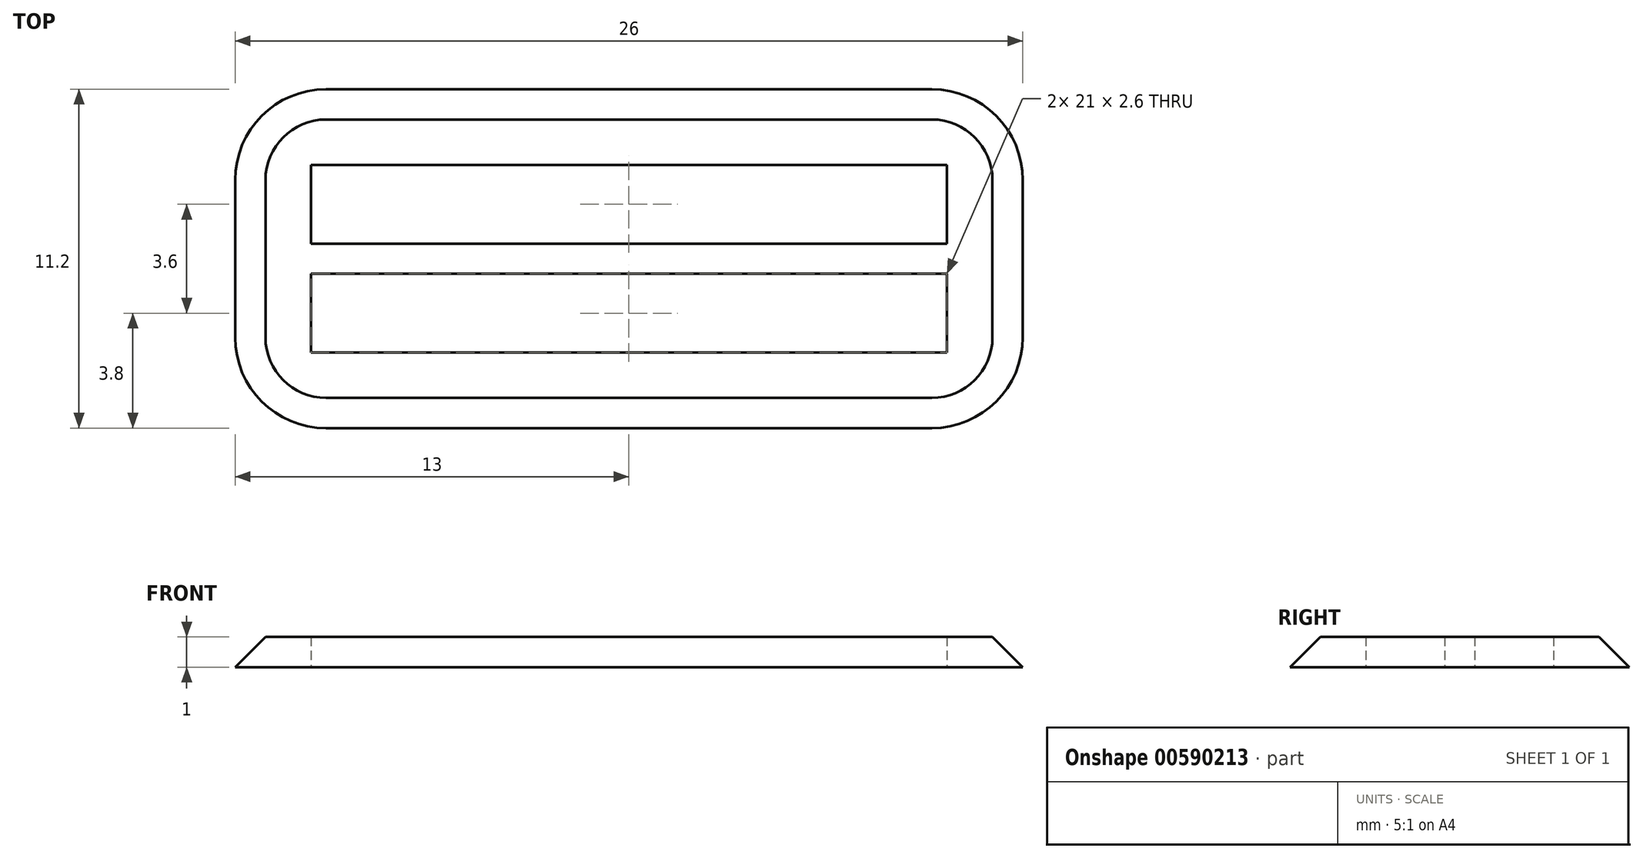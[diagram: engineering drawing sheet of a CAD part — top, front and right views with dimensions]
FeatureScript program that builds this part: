
annotation { "Feature Type Name" : "Feature", "Feature Type Description" : "" }
export const myFeature = defineFeature(function(context is Context, id is Id, definition is map)
    precondition{}
    {
        {
            var Q0;
            Q0=qCreatedBy(makeId("Top.planeOp"),FACE);
            var sketch = newSketch(context, id + "F0", { "sketchPlane" : qUnion([Q0])});
            skPoint(sketch, "E0.middle", {"position": v(0, 0) * mm});
            skLineSegment(sketch, "E1.bottom", {"start": v(-10.5, 3.1) * mm, "end": v(10.5, 3.1) * mm});
            skLineSegment(sketch, "E1.top", {"start": v(-10.5, 0.5) * mm, "end": v(10.5, 0.5) * mm});
            skLineSegment(sketch, "E1.left", {"start": v(-10.5, 3.1) * mm, "end": v(-10.5, 0.5) * mm});
            skLineSegment(sketch, "E1.right", {"start": v(10.5, 3.1) * mm, "end": v(10.5, 0.5) * mm});
            skPoint(sketch, "E1.middle", {"position": v(0, 1.8) * mm});
            skLineSegment(sketch, "E2.bottom", {"start": v(-10.5, -0.5) * mm, "end": v(10.5, -0.5) * mm});
            skLineSegment(sketch, "E2.top", {"start": v(-10.5, -3.1) * mm, "end": v(10.5, -3.1) * mm});
            skLineSegment(sketch, "E2.left", {"start": v(-10.5, -0.5) * mm, "end": v(-10.5, -3.1) * mm});
            skLineSegment(sketch, "E2.right", {"start": v(10.5, -0.5) * mm, "end": v(10.5, -3.1) * mm});
            skPoint(sketch, "E2.middle", {"position": v(0, -1.8) * mm});
            skLineSegment(sketch, "E3.bottom", {"start": v(-13, 5.6) * mm, "end": v(13, 5.6) * mm});
            skLineSegment(sketch, "E3.top", {"start": v(-13, -5.6) * mm, "end": v(13, -5.6) * mm});
            skLineSegment(sketch, "E3.left", {"start": v(-13, 5.6) * mm, "end": v(-13, -5.6) * mm});
            skLineSegment(sketch, "E3.right", {"start": v(13, 5.6) * mm, "end": v(13, -5.6) * mm});
            skSolve(sketch);
        }
        {
            var Q0;
            Q0=makeQuery(id+"F0.imprint","IMPRINT",FACE,{"disambiguationData":[TD([[makeQuery(id+"F0.imprint","IMPRINT",EDGE,{"derivedFrom":sQuery(id+"F0.wireOp",EDGE,"E1.bottom")}),1.0]])]});
            extrude(context, id + "F1", {"entities" : qUnion([Q0]), "depth" : 1 * mm, "offsetDistance" : 25 * mm});
        }
        {
            var Q0;
            Q0=makeQuery(id+"F1.opExtrude","SWEPT_EDGE",EDGE,{"disambiguationData":[OSD([sQuery(id+"F0.wireOp",EDGE,"E3.bottom"),sQuery(id+"F0.wireOp",EDGE,"E3.left")])]});
            var Q1;
            Q1=makeQuery(id+"F1.opExtrude","SWEPT_EDGE",EDGE,{"disambiguationData":[OSD([sQuery(id+"F0.wireOp",EDGE,"E3.top"),sQuery(id+"F0.wireOp",EDGE,"E3.left")])]});
            var Q2;
            Q2=makeQuery(id+"F1.opExtrude","SWEPT_EDGE",EDGE,{"disambiguationData":[OSD([sQuery(id+"F0.wireOp",EDGE,"E3.top"),sQuery(id+"F0.wireOp",EDGE,"E3.right")])]});
            var Q3;
            Q3=makeQuery(id+"F1.opExtrude","SWEPT_EDGE",EDGE,{"disambiguationData":[OSD([sQuery(id+"F0.wireOp",EDGE,"E3.bottom"),sQuery(id+"F0.wireOp",EDGE,"E3.right")])]});
            fillet(context, id + "F2", {"entities" : qUnion([Q0, Q1, Q2, Q3]), "radius" : 3 * mm, "tangentPropagation" : true, "allowEdgeOverflow" : false});
        }
        {
            var Q0;
            {var subQ0=sQuery(id+"F0.wireOp",EDGE,"E3.left");var subQ1=sQuery(id+"F0.wireOp",EDGE,"E3.top");Q0=makeQuery(id+"F2.opFillet","BLEND_EDGE",EDGE,{"blendedFrom":[makeQuery(id+"F1.opExtrude","SWEPT_EDGE",EDGE,{"disambiguationData":[OSD([subQ1,subQ0])]}),makeQuery(id+"F1.opExtrude","CAP_FACE",FACE,{"disambiguationData":[OSD([sQuery(id+"F0.wireOp",EDGE,"E1.bottom"),sQuery(id+"F0.wireOp",EDGE,"E1.top"),sQuery(id+"F0.wireOp",EDGE,"E1.left"),sQuery(id+"F0.wireOp",EDGE,"E1.right"),sQuery(id+"F0.wireOp",EDGE,"E2.bottom"),sQuery(id+"F0.wireOp",EDGE,"E2.top"),sQuery(id+"F0.wireOp",EDGE,"E2.left"),sQuery(id+"F0.wireOp",EDGE,"E2.right"),sQuery(id+"F0.wireOp",EDGE,"E3.bottom"),subQ1,subQ0,sQuery(id+"F0.wireOp",EDGE,"E3.right")])],"isStart":false})],"blendedInto":[makeQuery(id+"F1.opExtrude","CAP_FACE",FACE,{"disambiguationData":[OSD([sQuery(id+"F0.wireOp",EDGE,"E1.bottom"),sQuery(id+"F0.wireOp",EDGE,"E1.top"),sQuery(id+"F0.wireOp",EDGE,"E1.left"),sQuery(id+"F0.wireOp",EDGE,"E1.right"),sQuery(id+"F0.wireOp",EDGE,"E2.bottom"),sQuery(id+"F0.wireOp",EDGE,"E2.top"),sQuery(id+"F0.wireOp",EDGE,"E2.left"),sQuery(id+"F0.wireOp",EDGE,"E2.right"),sQuery(id+"F0.wireOp",EDGE,"E3.bottom"),subQ1,subQ0,sQuery(id+"F0.wireOp",EDGE,"E3.right")])],"isStart":false})]});}
            chamfer(context, id + "F3", {"entities" : qUnion([Q0]), "width" : 1 * mm, "tangentPropagation" : true});
        }
    });
